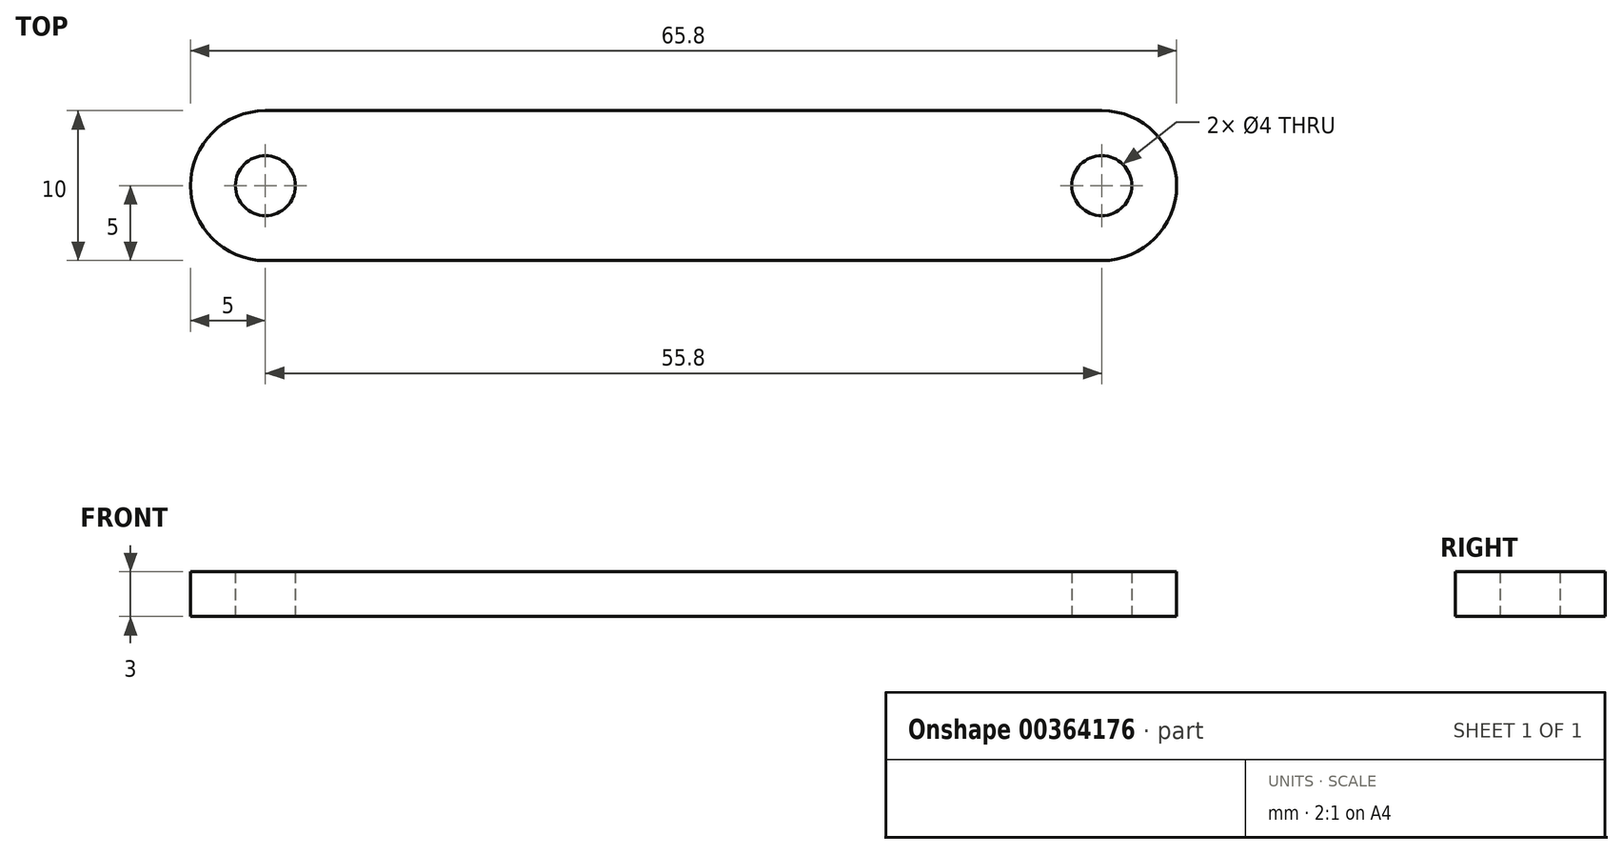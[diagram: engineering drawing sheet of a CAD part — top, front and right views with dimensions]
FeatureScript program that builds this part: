
annotation { "Feature Type Name" : "Feature", "Feature Type Description" : "" }
export const myFeature = defineFeature(function(context is Context, id is Id, definition is map)
    precondition{}
    {
        {
            var Q0;
            Q0=qCreatedBy(makeId("Top.planeOp"),FACE);
            var sketch = newSketch(context, id + "F0", { "sketchPlane" : qUnion([Q0])});
            skLineSegment(sketch, "E0.bottom", {"start": v(27.9, 5) * mm, "end": v(-27.9, 5) * mm});
            skLineSegment(sketch, "E0.top", {"start": v(27.9, -5) * mm, "end": v(-27.9, -5) * mm});
            skPoint(sketch, "E0.middle", {"position": v(0, 0) * mm});
            skCircle(sketch, "E1", {"center": v(-27.9, 0) * mm, "radius": 2 * mm});
            skCircle(sketch, "E2", {"center": v(27.9, 0) * mm, "radius": 2 * mm});
            skArc(sketch, "E3", {"start": v(-27.9, 5) * mm, "mid": v(-32.9, 0) * mm, "end": v(-27.9, -5) * mm});
            skArc(sketch, "E4", {"start": v(27.9, -5) * mm, "mid": v(32.9, 0) * mm, "end": v(27.9, 5) * mm});
            skSolve(sketch);
        }
        {
            var Q0;
            Q0=qSketchRegion(id+"F0",true);
            extrude(context, id + "F1", {"entities" : qUnion([Q0]), "depth" : 3 * mm});
        }
    });
